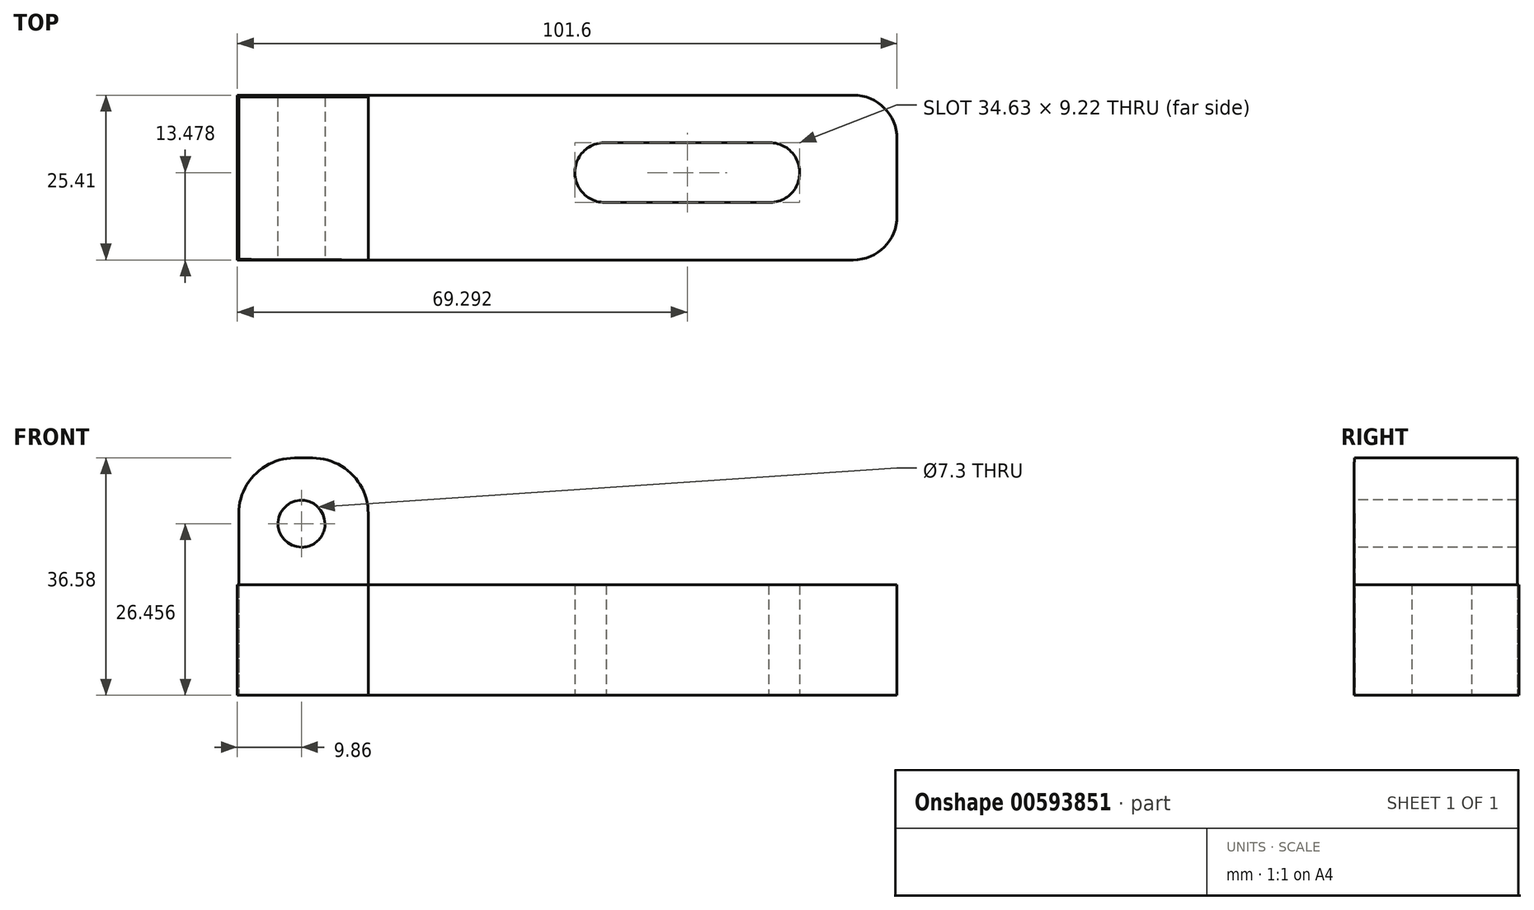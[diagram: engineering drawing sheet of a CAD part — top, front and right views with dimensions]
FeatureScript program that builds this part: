
annotation { "Feature Type Name" : "Feature", "Feature Type Description" : "" }
export const myFeature = defineFeature(function(context is Context, id is Id, definition is map)
    precondition{}
    {
        {
            var Q0;
            Q0=qCreatedBy(makeId("Top.planeOp"),FACE);
            var sketch = newSketch(context, id + "F0", { "sketchPlane" : qUnion([Q0])});
            skLineSegment(sketch, "E0.bottom", {"start": v(-50.8, 12.7) * mm, "end": v(50.8, 12.7) * mm});
            skLineSegment(sketch, "E0.top", {"start": v(-50.8, -12.7) * mm, "end": v(50.8, -12.7) * mm});
            skLineSegment(sketch, "E0.left", {"start": v(-50.8, 12.7) * mm, "end": v(-50.8, -12.7) * mm});
            skLineSegment(sketch, "E0.right", {"start": v(50.8, 12.7) * mm, "end": v(50.8, -12.7) * mm});
            skPoint(sketch, "E0.middle", {"position": v(0, 0) * mm});
            skLineSegment(sketch, "E1", {"start": v(31.2, 5.38) * mm, "end": v(6, 5.38) * mm});
            skLineSegment(sketch, "E2", {"start": v(31, -3.84) * mm, "end": v(5.79, -3.84) * mm});
            skArc(sketch, "E3", {"start": v(6, 5.38) * mm, "mid": v(1.18, 0.87) * mm, "end": v(5.79, -3.84) * mm});
            skArc(sketch, "E4", {"start": v(31, -3.84) * mm, "mid": v(35.8, 0.66) * mm, "end": v(31.2, 5.38) * mm});
            skSolve(sketch);
        }
        {
            var Q0;
            Q0=makeQuery(id+"F0.imprint","IMPRINT",FACE,{"disambiguationData":[TD([[makeQuery(id+"F0.imprint","IMPRINT",EDGE,{"derivedFrom":sQuery(id+"F0.wireOp",EDGE,"E0.bottom")}),-1.0]])]});
            extrude(context, id + "F1", {"entities" : qUnion([Q0]), "depth" : 17.02 * mm, "offsetDistance" : 25.4 * mm});
        }
        {
            var Q0;
            Q0=makeQuery(id+"F1.opExtrude","SWEPT_EDGE",EDGE,{"disambiguationData":[OSD([sQuery(id+"F0.wireOp",EDGE,"E0.top"),sQuery(id+"F0.wireOp",EDGE,"E0.right")])]});
            var Q1;
            Q1=makeQuery(id+"F1.opExtrude","SWEPT_EDGE",EDGE,{"disambiguationData":[OSD([sQuery(id+"F0.wireOp",EDGE,"E0.bottom"),sQuery(id+"F0.wireOp",EDGE,"E0.right")])]});
            fillet(context, id + "F2", {"entities" : qUnion([Q0, Q1]), "radius" : 6.75 * mm, "tangentPropagation" : true, "allowEdgeOverflow" : false});
        }
        {
            var Q0;
            Q0=qCreatedBy(makeId("Top.planeOp"),FACE);
            var sketch = newSketch(context, id + "F3", { "sketchPlane" : qUnion([Q0])});
            skLineSegment(sketch, "E5", {"start": v(-30.64, -12.7) * mm, "end": v(-30.64, 12.43) * mm});
            skLineSegment(sketch, "E6", {"start": v(-30.64, 12.43) * mm, "end": v(-50.6, 12.43) * mm});
            skLineSegment(sketch, "E7", {"start": v(-50.6, 12.43) * mm, "end": v(-50.6, -12.62) * mm});
            skLineSegment(sketch, "E8", {"start": v(-50.6, -12.62) * mm, "end": v(-30.64, -12.7) * mm});
            skSolve(sketch);
        }
        {
            var Q0;
            Q0 = qSketchRegion(id + "F3", true);
            extrude(context, id + "F4", {"entities" : qUnion([Q0]), "depth" : 36.58 * mm, "offsetDistance" : 25.4 * mm});
        }
        {
            var Q0;
            Q0=makeQuery(id+"F4.opExtrude","CAP_EDGE",EDGE,{"disambiguationData":[OSD([sQuery(id+"F3.wireOp",EDGE,"E5")])],"isStart":false});
            var Q1;
            Q1=makeQuery(id+"F4.opExtrude","CAP_EDGE",EDGE,{"disambiguationData":[OSD([sQuery(id+"F3.wireOp",EDGE,"E7")])],"isStart":false});
            fillet(context, id + "F5", {"entities" : qUnion([Q0, Q1]), "radius" : 8.58 * mm, "tangentPropagation" : true, "allowEdgeOverflow" : false});
        }
        {
            var Q0;
            Q0=qCreatedBy(makeId("Front.planeOp"),FACE);
            var sketch = newSketch(context, id + "F6", { "sketchPlane" : qUnion([Q0])});
            skCircle(sketch, "E9", {"center": v(-40.94, 26.46) * mm, "radius": 3.65 * mm});
            skSolve(sketch);
        }
        {
            var Q0;
            Q0 = qSketchRegion(id + "F6", true);
            extrude(context, id + "F7", {"entities" : qUnion([Q0]), "operationType" : NewBodyOperationType.REMOVE, "endBound" : BoundingType.SYMMETRIC, "oppositeDirection" : true, "depth" : 71.42 * mm, "offsetDistance" : 25.4 * mm});
        }
    });
